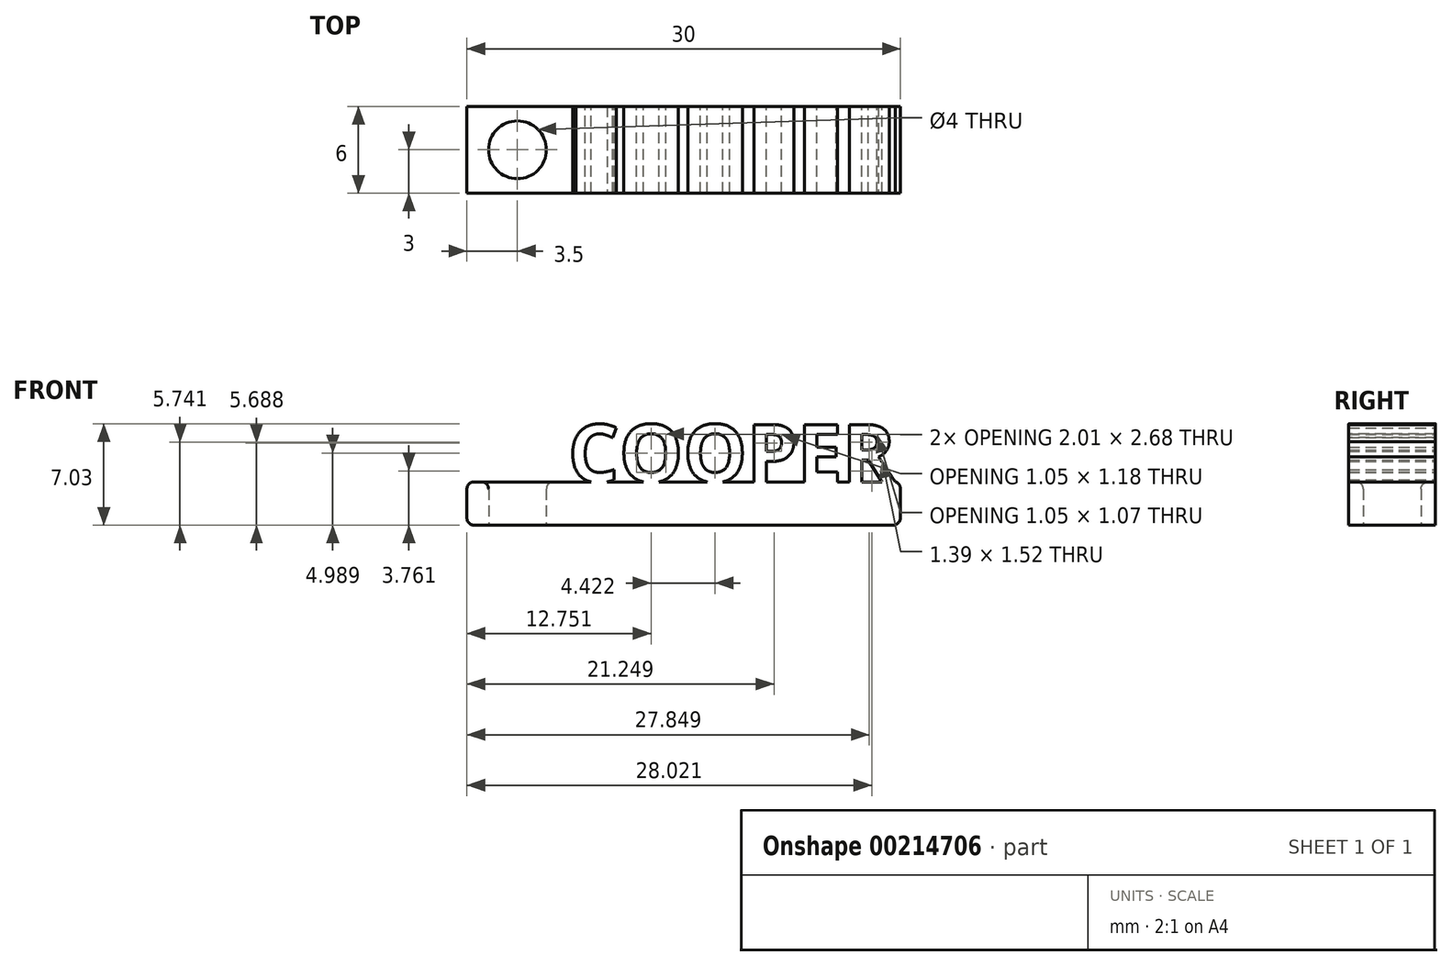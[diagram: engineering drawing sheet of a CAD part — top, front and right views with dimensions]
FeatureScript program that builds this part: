
annotation { "Feature Type Name" : "Feature", "Feature Type Description" : "" }
export const myFeature = defineFeature(function(context is Context, id is Id, definition is map)
    precondition{}
    {
        {
            var Q0;
            Q0=qCreatedBy(makeId("Front.planeOp"),FACE);
            var sketch = newSketch(context, id + "F0", { "sketchPlane" : qUnion([Q0])});
            skLineSegment(sketch, "E0.bottom", {"start": v(0, 0) * mm, "end": v(30, 0) * mm});
            skLineSegment(sketch, "E0.top", {"start": v(0, 3) * mm, "end": v(30, 3) * mm});
            skLineSegment(sketch, "E0.left", {"start": v(0, 0) * mm, "end": v(0, 3) * mm});
            skLineSegment(sketch, "E0.right", {"start": v(30, 0) * mm, "end": v(30, 3) * mm});
            skText(sketch, "E1", { "text": "COOPER", "fontName": "OpenSans-Bold.ttf"});
            const initialGuessF0  = {"E1": [0.007, 0.003, 1, 0, 0.004]};
            skSetInitialGuess(sketch, initialGuessF0);
            skSolve(sketch);
        }
        {
            var Q0;
            Q0=qCreatedBy(makeId("Top.planeOp"),FACE);
            var sketch = newSketch(context, id + "F1", { "sketchPlane" : qUnion([Q0])});
            skLineSegment(sketch, "E2", {"start": v(0, 0) * mm, "end": v(3.5, 0) * mm});
            skCircle(sketch, "E3", {"center": v(3.5, 0) * mm, "radius": 2 * mm});
            skSolve(sketch);
        }
        {
            var Q0;
            Q0 = qSketchRegion(id + "F0", true);
            extrude(context, id + "F2", {"entities" : qUnion([Q0]), "depth" : 3 * mm});
        }
        {
            var Q0;
            Q0=makeQuery(id+"F2.opExtrude","CAP_FACE",FACE,{"disambiguationData":[OSD([sQuery(id+"F0.wireOp",EDGE,"E0.bottom"),sQuery(id+"F0.wireOp",EDGE,"E0.top"),sQuery(id+"F0.wireOp",EDGE,"E0.left"),sQuery(id+"F0.wireOp",EDGE,"E0.right"),sQuery(id+"F0.wireOp",EDGE,"E1.sketch_text.stroke-5"),sQuery(id+"F0.wireOp",EDGE,"E1.sketch_text.stroke-6"),sQuery(id+"F0.wireOp",EDGE,"E1.sketch_text.stroke-16"),sQuery(id+"F0.wireOp",EDGE,"E1.sketch_text.stroke-17"),sQuery(id+"F0.wireOp",EDGE,"E1.sketch_text.stroke-30"),sQuery(id+"F0.wireOp",EDGE,"E1.sketch_text.stroke-31"),sQuery(id+"F0.wireOp",EDGE,"E1.sketch_text.stroke-54"),sQuery(id+"F0.wireOp",EDGE,"E1.sketch_text.stroke-59"),sQuery(id+"F0.wireOp",EDGE,"E1.sketch_text.stroke-79"),sQuery(id+"F0.wireOp",EDGE,"E1.sketch_text.stroke-87")])],"isStart":true});
            extrude(context, id + "F3", {"entities" : qUnion([Q0]), "operationType" : NewBodyOperationType.ADD, "depth" : 3 * mm});
        }
        {
            var Q0;
            Q0=makeQuery(id+"F1.imprint","IMPRINT",FACE,{"disambiguationData":[TD([[makeQuery(id+"F1.imprint","IMPRINT",EDGE,{"derivedFrom":sQuery(id+"F1.wireOp",EDGE,"E3")}),1.0]])]});
            var Q1;
            Q1=sQuery(id+"F1.wireOp",EDGE,"E3");
            extrude(context, id + "F4", {"entities" : qUnion([Q0]), "operationType" : NewBodyOperationType.REMOVE, "surfaceEntities" : qUnion([Q1]), "depth" : 10 * mm});
        }
        {
            var Q0;
            {var subQ0=sQuery(id+"F0.wireOp",EDGE,"E0.right");var subQ1=sQuery(id+"F0.wireOp",EDGE,"E0.bottom");Q0=makeQuery(id+"F3.boolean.opBoolean","MERGE",EDGE,{"derivedFrom":[makeQuery(id+"F2.opExtrude","SWEPT_EDGE",EDGE,{"disambiguationData":[OSD([subQ1,subQ0])]}),makeQuery(id+"F3.opExtrude","SWEPT_EDGE",EDGE,{"disambiguationData":[OSD([subQ1,subQ0])]})]});}
            var Q1;
            {var subQ0=sQuery(id+"F0.wireOp",EDGE,"E0.right");var subQ1=sQuery(id+"F0.wireOp",EDGE,"E0.top");Q1=makeQuery(id+"F3.boolean.opBoolean","MERGE",EDGE,{"derivedFrom":[makeQuery(id+"F2.opExtrude","SWEPT_EDGE",EDGE,{"disambiguationData":[OSD([subQ1,subQ0])]}),makeQuery(id+"F3.opExtrude","SWEPT_EDGE",EDGE,{"disambiguationData":[OSD([subQ1,subQ0])]})]});}
            fillet(context, id + "F5", {"entities" : qUnion([Q0, Q1]), "radius" : 0.5 * mm, "tangentPropagation" : true, "allowEdgeOverflow" : false});
        }
        {
            var Q0;
            {var subQ0=sQuery(id+"F0.wireOp",EDGE,"E0.left");var subQ1=sQuery(id+"F0.wireOp",EDGE,"E0.top");Q0=makeQuery(id+"F3.boolean.opBoolean","MERGE",EDGE,{"derivedFrom":[makeQuery(id+"F2.opExtrude","SWEPT_EDGE",EDGE,{"disambiguationData":[OSD([subQ1,subQ0])]}),makeQuery(id+"F3.opExtrude","SWEPT_EDGE",EDGE,{"disambiguationData":[OSD([subQ1,subQ0])]})]});}
            var Q1;
            {var subQ0=sQuery(id+"F0.wireOp",EDGE,"E0.left");var subQ1=sQuery(id+"F0.wireOp",EDGE,"E0.bottom");Q1=makeQuery(id+"F3.boolean.opBoolean","MERGE",EDGE,{"derivedFrom":[makeQuery(id+"F2.opExtrude","SWEPT_EDGE",EDGE,{"disambiguationData":[OSD([subQ1,subQ0])]}),makeQuery(id+"F3.opExtrude","SWEPT_EDGE",EDGE,{"disambiguationData":[OSD([subQ1,subQ0])]})]});}
            fillet(context, id + "F6", {"entities" : qUnion([Q0, Q1]), "radius" : 0.5 * mm, "tangentPropagation" : true, "allowEdgeOverflow" : false});
        }
        {
            var Q0;
            {var subQ0=sQuery(id+"F0.wireOp",EDGE,"E0.top");var subQ1=makeQuery(id+"F0.imprint","IMPRINT",EDGE,{"disambiguationData":[TD([[makeQuery(id+"F0.imprint","INTERSECT",VERTEX,{"derivedFrom":[subQ0,sQuery(id+"F0.wireOp",EDGE,"E0.left")]}),-1.0]])],"derivedFrom":subQ0});Q0=makeQuery(id+"F4.boolean.opBoolean","INTERSECT",EDGE,{"derivedFrom":[makeQuery(id+"F3.boolean.opBoolean","MERGE",FACE,{"derivedFrom":[makeQuery(id+"F2.opExtrude","SWEPT_FACE",FACE,{"disambiguationData":[OSD([subQ0]),TDD([subQ1])]}),makeQuery(id+"F3.opExtrude","SWEPT_FACE",FACE,{"disambiguationData":[OSD([subQ0]),TDD([makeQuery(id+"F2.opExtrude","CAP_EDGE",EDGE,{"disambiguationData":[OSD([subQ0]),TDD([subQ1])],"isStart":true})])]})]}),makeQuery(id+"F4.opExtrude","SWEPT_FACE",FACE,{"disambiguationData":[OSD([sQuery(id+"F1.wireOp",EDGE,"E3")])]})]});}
            var Q1;
            Q1=makeQuery(id+"F4.boolean.opBoolean","COPY",EDGE,{"derivedFrom":makeQuery(id+"F4.opExtrude","CAP_EDGE",EDGE,{"disambiguationData":[OSD([sQuery(id+"F1.wireOp",EDGE,"E3")])],"isStart":true})});
            fillet(context, id + "F7", {"entities" : qUnion([Q0, Q1]), "radius" : 0.5 * mm, "tangentPropagation" : true, "allowEdgeOverflow" : false});
        }
    });
